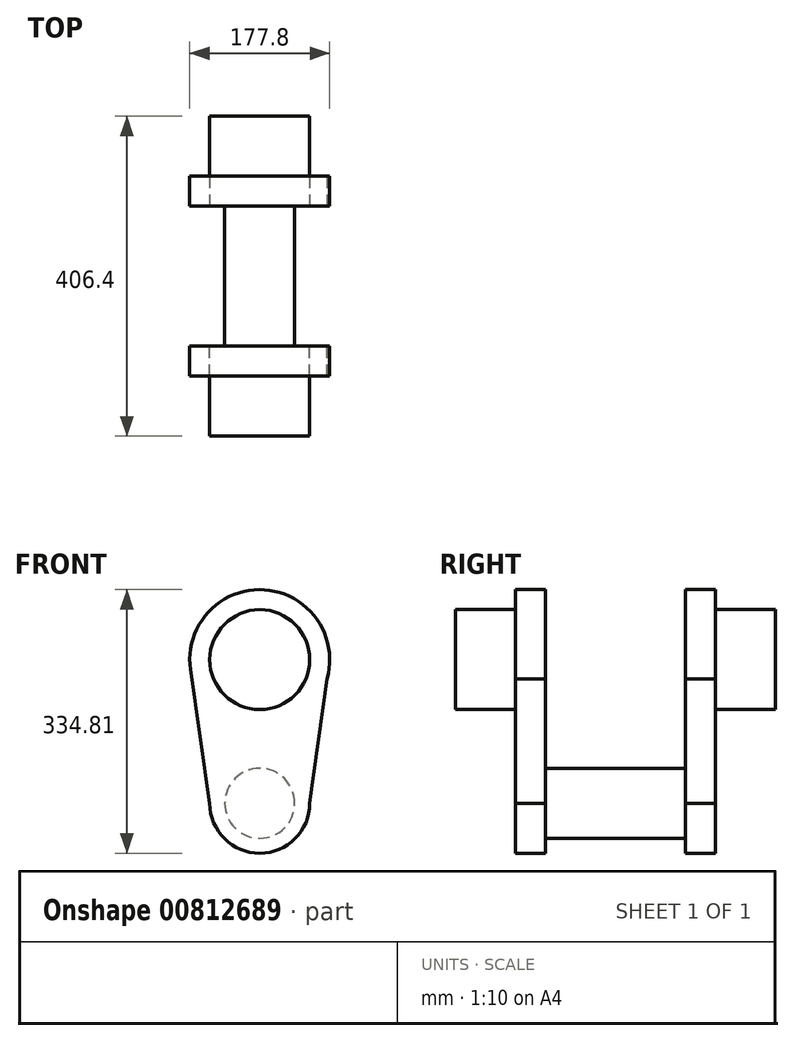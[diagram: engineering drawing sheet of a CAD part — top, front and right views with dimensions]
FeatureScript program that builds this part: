
annotation { "Feature Type Name" : "Feature", "Feature Type Description" : "" }
export const myFeature = defineFeature(function(context is Context, id is Id, definition is map)
    precondition{}
    {
        {
            var Q0;
            Q0=qCreatedBy(makeId("Front.planeOp"),FACE);
            var sketch = newSketch(context, id + "F0", { "sketchPlane" : qUnion([Q0])});
            skArc(sketch, "E0", {"start": v(85.52, -24.29) * mm, "mid": v(5.93, 88.7) * mm, "end": v(-87.99, -12.7) * mm});
            skArc(sketch, "E1", {"start": v(-63.5, -182.41) * mm, "mid": v(0, -245.91) * mm, "end": v(63.5, -182.41) * mm});
            skLineSegment(sketch, "E2", {"start": v(-63.5, -182.41) * mm, "end": v(-89.82, 0) * mm});
            skLineSegment(sketch, "E3", {"start": v(88.9, 0) * mm, "end": v(63.5, -182.41) * mm});
            skSolve(sketch);
        }
        {
            var Q0;
            Q0 = qSketchRegion(id + "F0", true);
            extrude(context, id + "F1", {"entities" : qUnion([Q0]), "depth" : 38.1 * mm, "offsetDistance" : 25.4 * mm});
        }
        {
            var Q0;
            Q0=makeQuery(id+"F1.opExtrude","CAP_FACE",FACE,{"disambiguationData":[OSD([sQuery(id+"F0.wireOp",EDGE,"E0"),sQuery(id+"F0.wireOp",EDGE,"E1"),sQuery(id+"F0.wireOp",EDGE,"E2"),sQuery(id+"F0.wireOp",EDGE,"E3")])],"isStart":false});
            var sketch = newSketch(context, id + "F2", { "sketchPlane" : qUnion([Q0])});
            skCircle(sketch, "E4", {"center": v(0, 0) * mm, "radius": 63.5 * mm});
            skSolve(sketch);
        }
        {
            var Q0;
            Q0=makeQuery(id+"F2.imprint","IMPRINT",FACE,{"disambiguationData":[TD([[makeQuery(id+"F2.imprint","IMPRINT",EDGE,{"derivedFrom":sQuery(id+"F2.wireOp",EDGE,"E4")}),1.0]])]});
            extrude(context, id + "F3", {"entities" : qUnion([Q0]), "operationType" : NewBodyOperationType.ADD, "depth" : 76.2 * mm, "offsetDistance" : 25.4 * mm});
        }
        {
            var Q0;
            Q0=makeQuery(id+"F1.opExtrude","CAP_FACE",FACE,{"disambiguationData":[OSD([sQuery(id+"F0.wireOp",EDGE,"E0"),sQuery(id+"F0.wireOp",EDGE,"E1"),sQuery(id+"F0.wireOp",EDGE,"E2"),sQuery(id+"F0.wireOp",EDGE,"E3")])],"isStart":true});
            var sketch = newSketch(context, id + "F4", { "sketchPlane" : qUnion([Q0])});
            skCircle(sketch, "E5", {"center": v(0, -182.41) * mm, "radius": 44.45 * mm});
            skSolve(sketch);
        }
        {
            var Q0;
            Q0=makeQuery(id+"F4.imprint","IMPRINT",FACE,{"disambiguationData":[TD([[makeQuery(id+"F4.imprint","IMPRINT",EDGE,{"derivedFrom":sQuery(id+"F4.wireOp",EDGE,"E5")}),1.0]])]});
            extrude(context, id + "F5", {"entities" : qUnion([Q0]), "operationType" : NewBodyOperationType.ADD, "depth" : 88.9 * mm, "offsetDistance" : 25.4 * mm});
        }
        {
            var Q0;
            Q0=makeQuery(id+"F1.opExtrude","SWEPT_BODY",BODY,{"disambiguationData":[OSD([sQuery(id+"F0.wireOp",EDGE,"E0"),sQuery(id+"F0.wireOp",EDGE,"E1"),sQuery(id+"F0.wireOp",EDGE,"E2"),sQuery(id+"F0.wireOp",EDGE,"E3")])]});
            var Q1;
            Q1=makeQuery(id+"F5.opExtrude","CAP_FACE",FACE,{"disambiguationData":[OSD([sQuery(id+"F4.wireOp",EDGE,"E5")])],"isStart":false});
            mirror(context, id + "F6", {"operationType" : NewBodyOperationType.ADD, "entities" : qUnion([Q0]), "mirrorPlane" : qUnion([Q1])});
        }
    });
